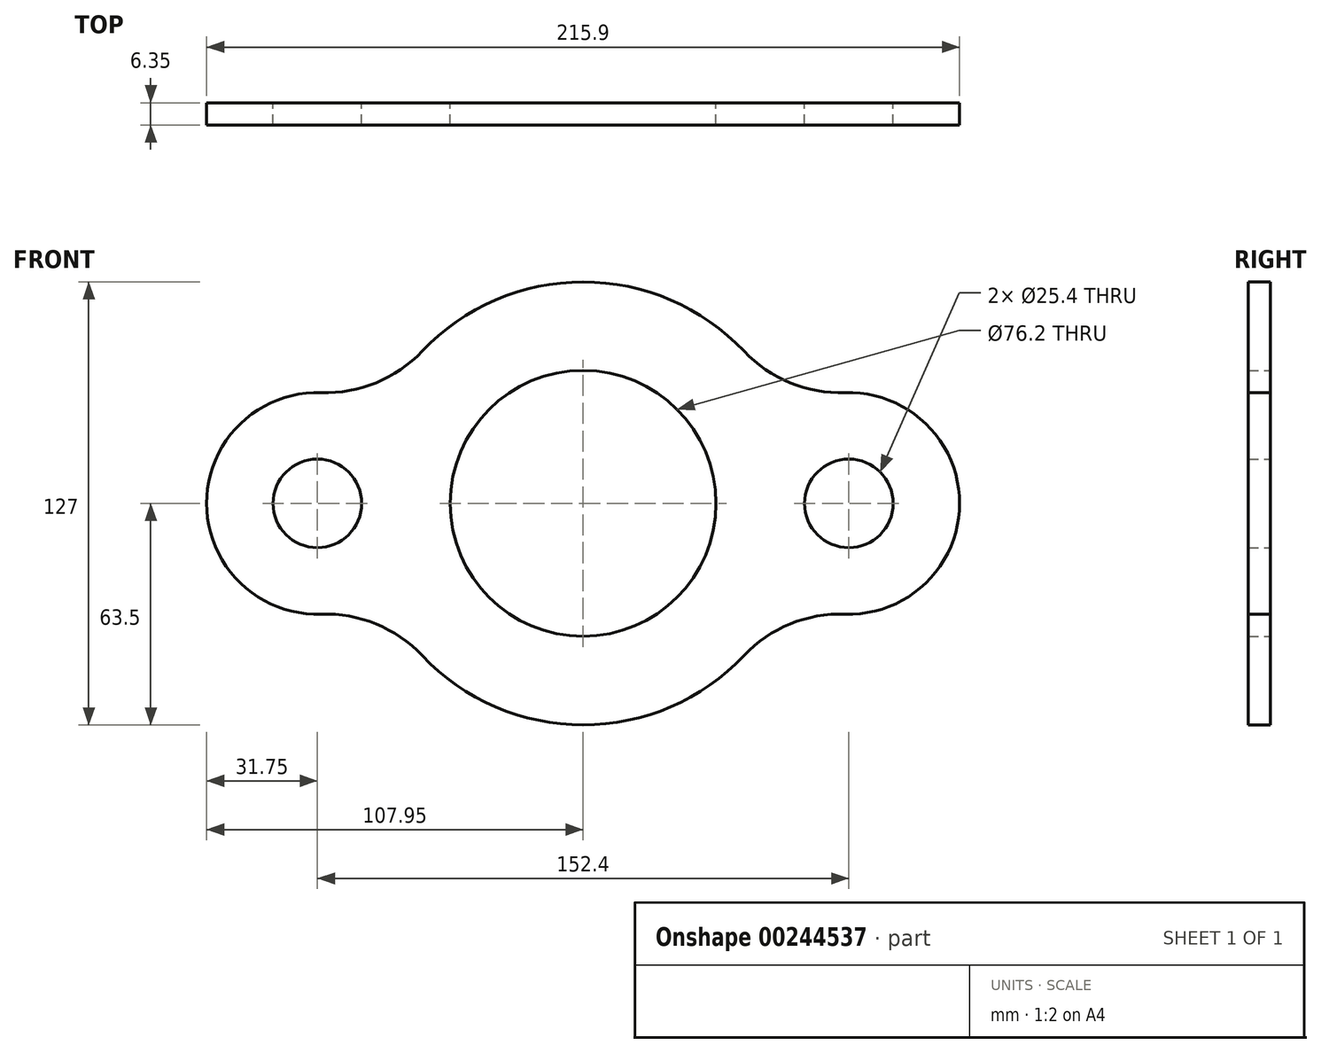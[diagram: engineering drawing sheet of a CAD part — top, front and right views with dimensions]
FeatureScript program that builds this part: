
annotation { "Feature Type Name" : "Feature", "Feature Type Description" : "" }
export const myFeature = defineFeature(function(context is Context, id is Id, definition is map)
    precondition{}
    {
        {
            var Q0;
            Q0=qCreatedBy(makeId("Front.planeOp"),FACE);
            var sketch = newSketch(context, id + "F0", { "sketchPlane" : qUnion([Q0])});
            skCircle(sketch, "E0", {"center": v(0, 0) * mm, "radius": 38.1 * mm});
            skCircle(sketch, "E1", {"center": v(-76.2, 0) * mm, "radius": 12.7 * mm});
            skCircle(sketch, "E2", {"center": v(76.2, 0) * mm, "radius": 12.7 * mm});
            skArc(sketch, "E3", {"start": v(75.12, -31.73) * mm, "mid": v(107.95, 0) * mm, "end": v(75.12, 31.73) * mm});
            skArc(sketch, "E4", {"start": v(-75.12, 31.73) * mm, "mid": v(-107.95, 0) * mm, "end": v(-75.12, -31.73) * mm});
            skArc(sketch, "E5", {"start": v(-46.14, -43.63) * mm, "mid": v(0, -63.5) * mm, "end": v(46.14, -43.63) * mm});
            skArc(sketch, "E6", {"start": v(-75.12, 31.73) * mm, "mid": v(-59.35, 34.56) * mm, "end": v(-46.14, 43.63) * mm});
            skArc(sketch, "E7", {"start": v(46.14, 43.63) * mm, "mid": v(59.35, 34.56) * mm, "end": v(75.12, 31.73) * mm});
            skArc(sketch, "E8", {"start": v(-46.14, -43.63) * mm, "mid": v(-59.35, -34.56) * mm, "end": v(-75.12, -31.73) * mm});
            skArc(sketch, "E9", {"start": v(75.12, -31.73) * mm, "mid": v(59.35, -34.56) * mm, "end": v(46.14, -43.63) * mm});
            skArc(sketch, "E10.trimOffspring", {"start": v(46.14, 43.63) * mm, "mid": v(0, 63.5) * mm, "end": v(-46.14, 43.63) * mm});
            skPoint(sketch, "E11.start.orphan", {"position": v(0, -56.18) * mm});
            skSolve(sketch);
        }
        {
            var Q0;
            Q0=makeQuery(id+"F0.imprint","IMPRINT",FACE,{"disambiguationData":[TD([[makeQuery(id+"F0.imprint","IMPRINT",EDGE,{"derivedFrom":sQuery(id+"F0.wireOp",EDGE,"E0")}),-1.0]])]});
            extrude(context, id + "F1", {"entities" : qUnion([Q0]), "depth" : 6.35 * mm});
        }
    });
